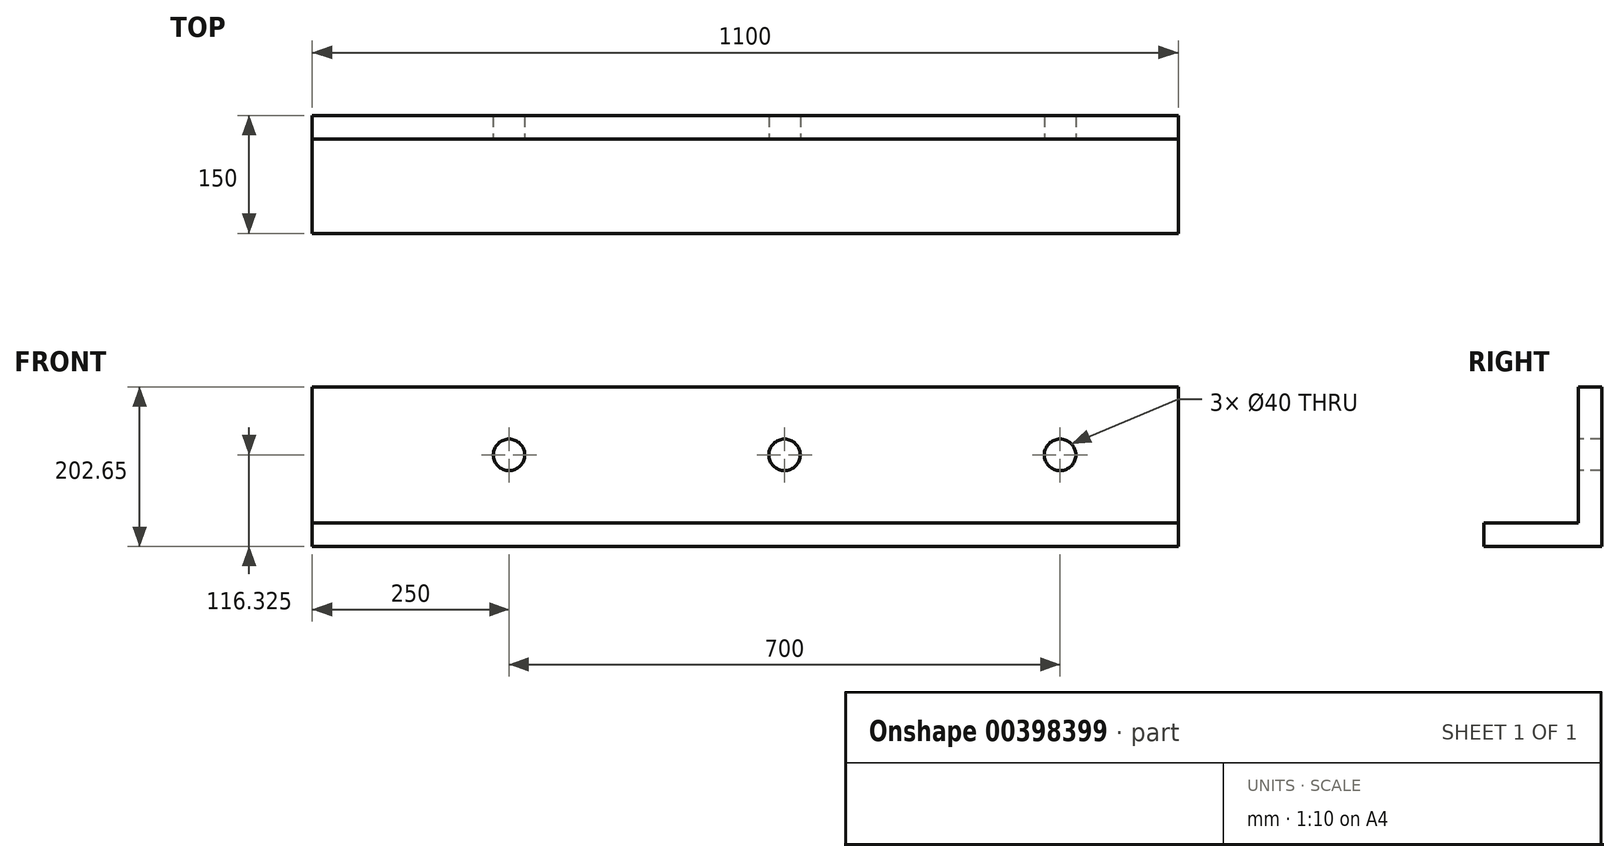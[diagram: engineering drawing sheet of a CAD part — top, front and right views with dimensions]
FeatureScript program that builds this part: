
annotation { "Feature Type Name" : "Feature", "Feature Type Description" : "" }
export const myFeature = defineFeature(function(context is Context, id is Id, definition is map)
    precondition{}
    {
        {
            var Q0;
            Q0=qCreatedBy(makeId("Right.planeOp"),FACE);
            var sketch = newSketch(context, id + "F0", { "sketchPlane" : qUnion([Q0])});
            skLineSegment(sketch, "E0.bottom", {"start": v(0, 0) * mm, "end": v(-150, 0) * mm});
            skLineSegment(sketch, "E0.top", {"start": v(0, -30) * mm, "end": v(-150, -30) * mm});
            skLineSegment(sketch, "E0.left", {"start": v(0, 0) * mm, "end": v(0, -30) * mm});
            skLineSegment(sketch, "E0.right", {"start": v(-150, 0) * mm, "end": v(-150, -30) * mm});
            skLineSegment(sketch, "E1.bottom", {"start": v(0, 0) * mm, "end": v(-30, 0) * mm});
            skLineSegment(sketch, "E1.top", {"start": v(0, 172.65) * mm, "end": v(-30, 172.65) * mm});
            skLineSegment(sketch, "E1.left", {"start": v(0, 0) * mm, "end": v(0, 172.65) * mm});
            skLineSegment(sketch, "E1.right", {"start": v(-30, 0) * mm, "end": v(-30, 172.65) * mm});
            skSolve(sketch);
        }
        {
            var Q0;
            Q0 = qSketchRegion(id + "F0", true);
            extrude(context, id + "F1", {"entities" : qUnion([Q0]), "depth" : 1100 * mm});
        }
        {
            var Q0;
            Q0=makeQuery(id+"F1.opExtrude","SWEPT_FACE",FACE,{"disambiguationData":[OSD([sQuery(id+"F0.wireOp",EDGE,"E1.right")])]});
            var sketch = newSketch(context, id + "F2", { "sketchPlane" : qUnion([Q0])});
            skCircle(sketch, "E2", {"center": v(250, 86.33) * mm, "radius": 20 * mm});
            skCircle(sketch, "E3.1.0.0", {"center": v(600, 86.33) * mm, "radius": 20 * mm});
            skCircle(sketch, "E3.2.0.0", {"center": v(950, 86.33) * mm, "radius": 20 * mm});
            skLineSegment(sketch, "E3.direction1", {"start": v(250, 86.33) * mm, "end": v(600, 86.33) * mm, "construction": true});
            skLineSegment(sketch, "E4", {"start": v(1100, 86.33) * mm, "end": v(0, 86.33) * mm, "construction": true});
            skCircle(sketch, "E5.0.3.0", {"center": v(1300, 86.33) * mm, "radius": 20 * mm});
            skSolve(sketch);
        }
        {
            var Q0;
            Q0 = qSketchRegion(id + "F2", true);
            extrude(context, id + "F3", {"entities" : qUnion([Q0]), "operationType" : NewBodyOperationType.REMOVE, "endBound" : BoundingType.THROUGH_ALL, "oppositeDirection" : true, "depth" : 25 * mm});
        }
    });
